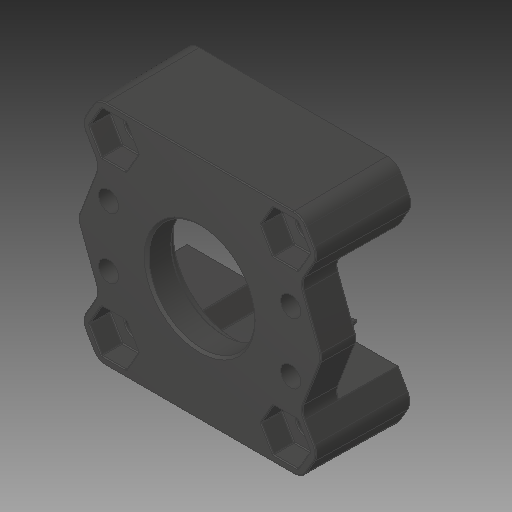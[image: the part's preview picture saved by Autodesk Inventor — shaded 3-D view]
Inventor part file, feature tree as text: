
AUTODESK INVENTOR PART (.ipt)
format: ipt  version: 2018 (Build 220112000, 112)  size: 2,103,808 bytes
history: native  units: in
note: dims shown in document units (in); Inventor stores cm internally (conversion verified against a paired STEP export)
features: chamfer x1
ambient origin geometry x8: Origin, YZ Plane, XZ Plane, XY Plane, X Axis, Y Axis, Z Axis, Center Point
bodies: Solid1 (feature_tree)
feature tree (1):
  chamfer  "Chamfer1"  [1 undecoded]
note: 1 required parameter value undecoded (feature->parameter linkage not recoverable at this tier; creation-order binding heuristic only, values carry confidence <= 0.55)
